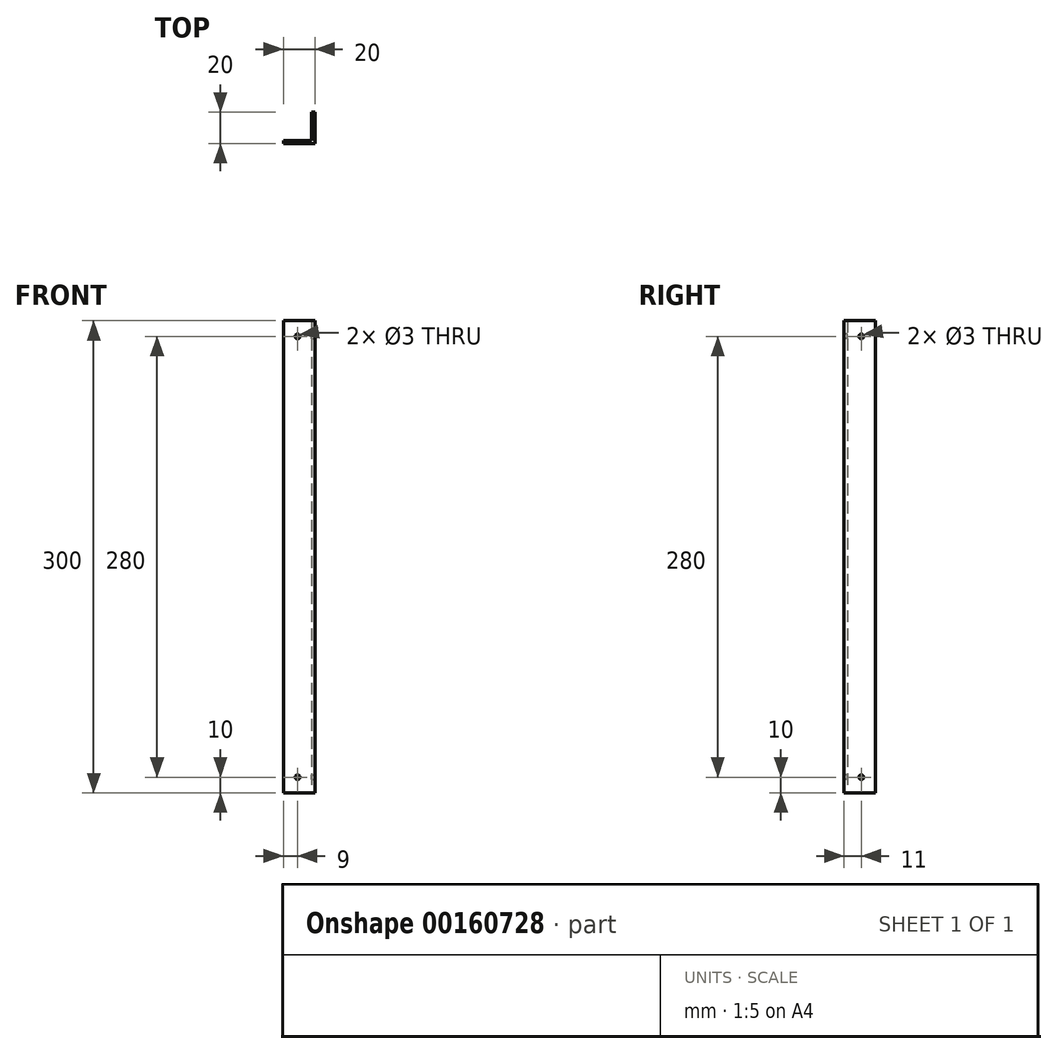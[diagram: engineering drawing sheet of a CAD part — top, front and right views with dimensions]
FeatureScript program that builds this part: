
annotation { "Feature Type Name" : "Feature", "Feature Type Description" : "" }
export const myFeature = defineFeature(function(context is Context, id is Id, definition is map)
    precondition{}
    {
        {
            var Q0;
            Q0=qCreatedBy(makeId("Top.planeOp"),FACE);
            var sketch = newSketch(context, id + "F0", { "sketchPlane" : qUnion([Q0])});
            skLineSegment(sketch, "E0", {"start": v(0, 0) * mm, "end": v(0, 20) * mm});
            skLineSegment(sketch, "E1", {"start": v(0, 20) * mm, "end": v(-2, 20) * mm});
            skLineSegment(sketch, "E2", {"start": v(-2, 20) * mm, "end": v(-2, 2) * mm});
            skLineSegment(sketch, "E3", {"start": v(-2, 2) * mm, "end": v(-20, 2) * mm});
            skLineSegment(sketch, "E4", {"start": v(-20, 2) * mm, "end": v(-20, 0) * mm});
            skLineSegment(sketch, "E5", {"start": v(-20, 0) * mm, "end": v(0, 0) * mm});
            skSolve(sketch);
        }
        {
            var Q0;
            Q0=makeQuery(id+"F0.imprint","IMPRINT",FACE,{"disambiguationData":[TD([[makeQuery(id+"F0.imprint","IMPRINT",EDGE,{"derivedFrom":sQuery(id+"F0.wireOp",EDGE,"E0")}),1.0]])]});
            extrude(context, id + "F1", {"entities" : qUnion([Q0]), "endBound" : BoundingType.SYMMETRIC, "depth" : 300 * mm});
        }
        {
            var Q0;
            Q0=makeQuery(id+"F1.opExtrude","SWEPT_FACE",FACE,{"disambiguationData":[OSD([sQuery(id+"F0.wireOp",EDGE,"E0")])]});
            var sketch = newSketch(context, id + "F2", { "sketchPlane" : qUnion([Q0])});
            skCircle(sketch, "E6", {"center": v(11, 140) * mm, "radius": 1.5 * mm});
            skCircle(sketch, "E7", {"center": v(11, -140) * mm, "radius": 1.5 * mm});
            skSolve(sketch);
        }
        {
            var Q0;
            Q0 = qSketchRegion(id + "F2", true);
            extrude(context, id + "F3", {"entities" : qUnion([Q0]), "operationType" : NewBodyOperationType.REMOVE, "endBound" : BoundingType.THROUGH_ALL, "oppositeDirection" : true, "depth" : 25 * mm});
        }
        {
            var Q0;
            Q0=makeQuery(id+"F1.opExtrude","SWEPT_FACE",FACE,{"disambiguationData":[OSD([sQuery(id+"F0.wireOp",EDGE,"E5")])]});
            var sketch = newSketch(context, id + "F4", { "sketchPlane" : qUnion([Q0])});
            skCircle(sketch, "E8", {"center": v(-11, 140) * mm, "radius": 1.5 * mm});
            skCircle(sketch, "E9", {"center": v(-11, -140) * mm, "radius": 1.5 * mm});
            skSolve(sketch);
        }
        {
            var Q0;
            Q0 = qSketchRegion(id + "F4", true);
            extrude(context, id + "F5", {"entities" : qUnion([Q0]), "operationType" : NewBodyOperationType.REMOVE, "endBound" : BoundingType.THROUGH_ALL, "oppositeDirection" : true, "depth" : 25 * mm});
        }
    });
